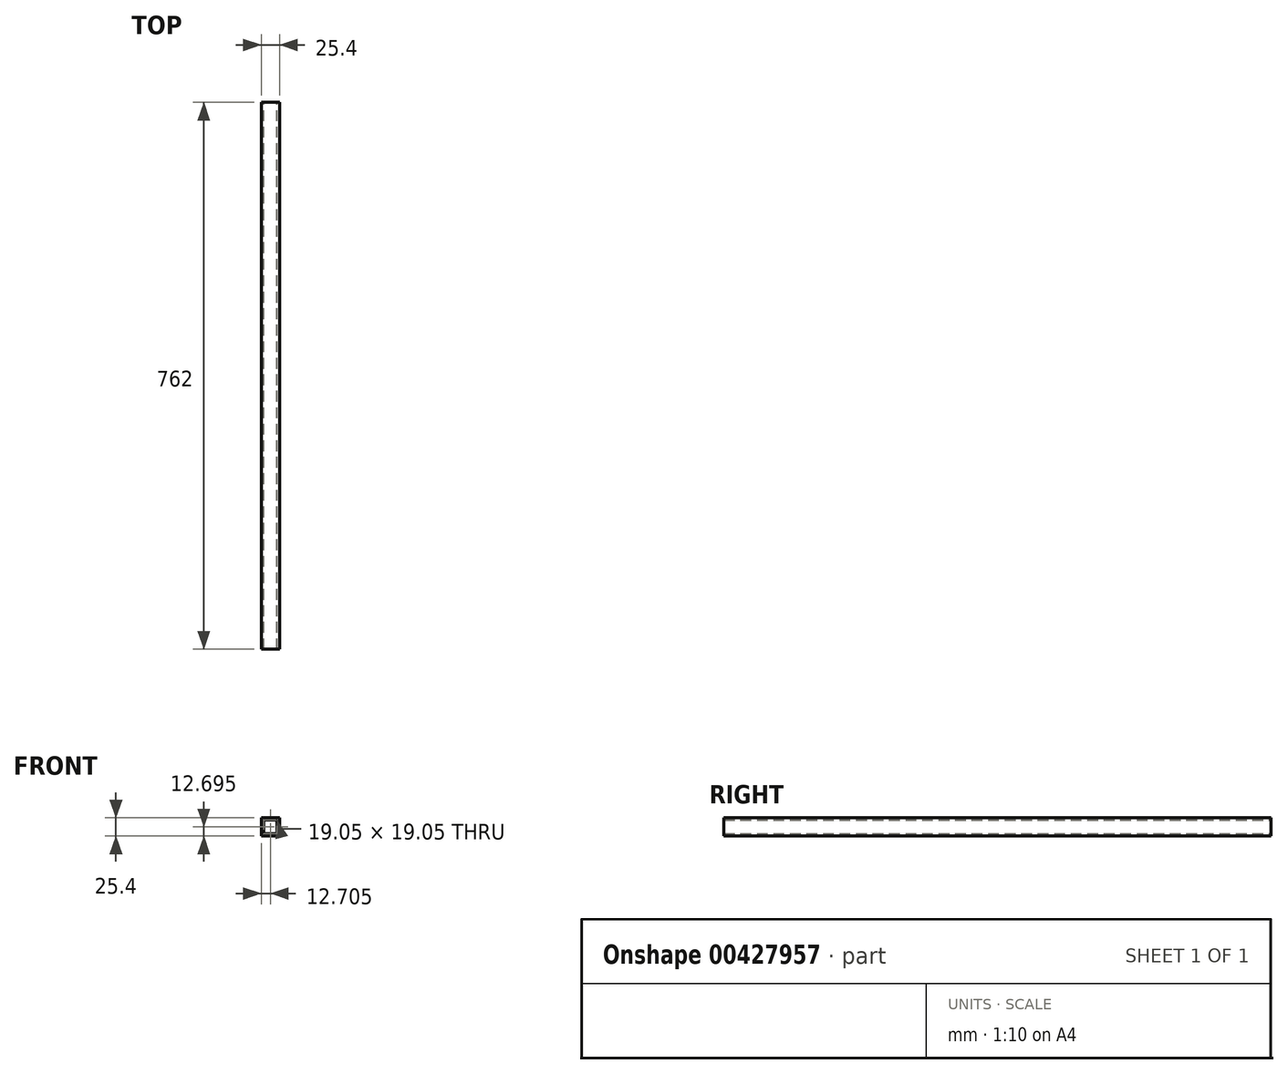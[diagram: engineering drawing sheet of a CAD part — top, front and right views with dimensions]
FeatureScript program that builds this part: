
annotation { "Feature Type Name" : "Feature", "Feature Type Description" : "" }
export const myFeature = defineFeature(function(context is Context, id is Id, definition is map)
    precondition{}
    {
        {
            var Q0;
            Q0=qCreatedBy(makeId("Front.planeOp"),FACE);
            var sketch = newSketch(context, id + "F0", { "sketchPlane" : qUnion([Q0])});
            skLineSegment(sketch, "E0.bottom", {"start": v(-22.23, 22.23) * mm, "end": v(3.17, 22.23) * mm});
            skLineSegment(sketch, "E0.top", {"start": v(-22.23, -3.18) * mm, "end": v(3.18, -3.18) * mm});
            skLineSegment(sketch, "E0.left", {"start": v(-22.23, 22.23) * mm, "end": v(-22.23, -3.18) * mm});
            skLineSegment(sketch, "E0.right", {"start": v(3.17, 22.23) * mm, "end": v(3.18, -3.18) * mm});
            skLineSegment(sketch, "E1.bottom", {"start": v(-19.05, 19.05) * mm, "end": v(0, 19.05) * mm});
            skLineSegment(sketch, "E1.top", {"start": v(-19.05, 0) * mm, "end": v(0, 0) * mm});
            skLineSegment(sketch, "E1.left", {"start": v(-19.05, 19.05) * mm, "end": v(-19.05, 0) * mm});
            skLineSegment(sketch, "E1.right", {"start": v(0, 19.05) * mm, "end": v(0, 0) * mm});
            skSolve(sketch);
        }
        {
            var Q0;
            Q0=qSketchRegion(id+"F0",true);
            extrude(context, id + "F1", {"entities" : qUnion([Q0]), "depth" : 762 * mm});
        }
    });
